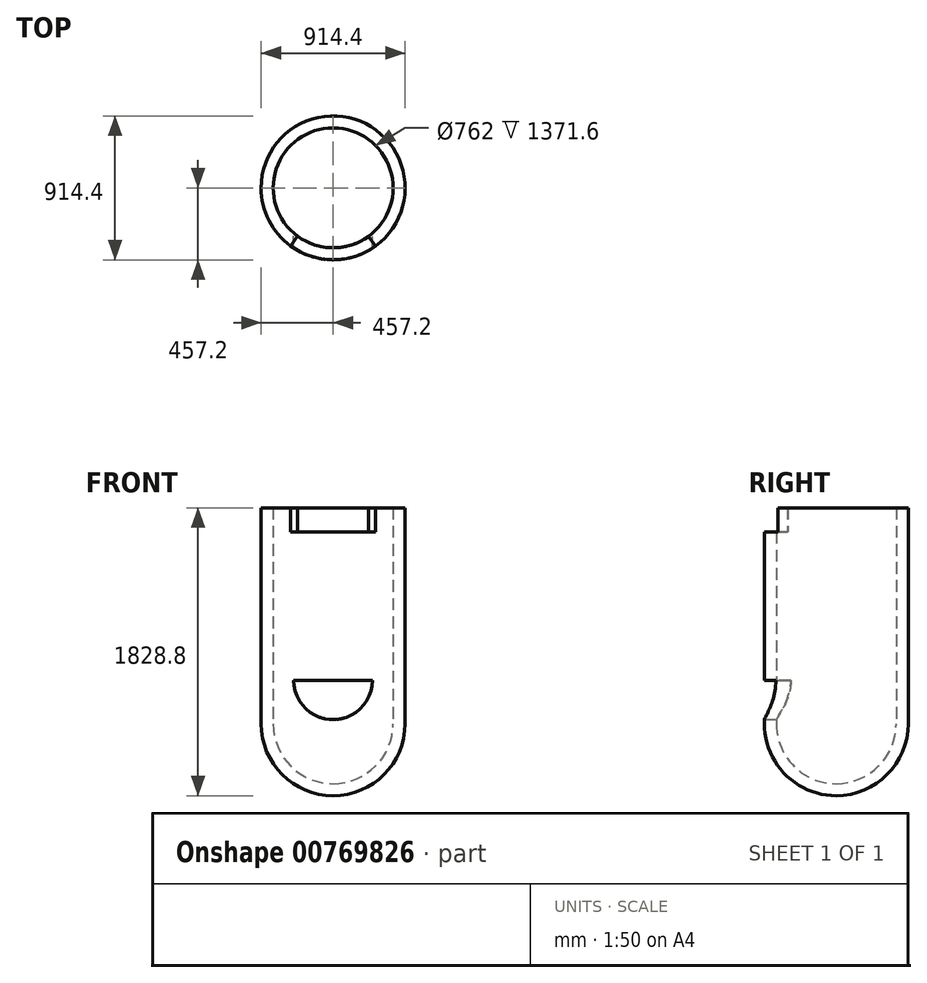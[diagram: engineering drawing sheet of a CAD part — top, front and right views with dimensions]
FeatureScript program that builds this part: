
annotation { "Feature Type Name" : "Feature", "Feature Type Description" : "" }
export const myFeature = defineFeature(function(context is Context, id is Id, definition is map)
    precondition{}
    {
        {
            var Q0;
            Q0=qCreatedBy(makeId("Top.planeOp"),FACE);
            var sketch = newSketch(context, id + "F0", { "sketchPlane" : qUnion([Q0])});
            skCircle(sketch, "E0", {"center": v(0, 0) * mm, "radius": 457.2 * mm});
            skCircle(sketch, "E1", {"center": v(0, 0) * mm, "radius": 381 * mm});
            skSolve(sketch);
        }
        {
            var Q0;
            Q0 = qSketchRegion(id + "F0", true);
            var Q1;
            Q1=makeQuery(id+"F0.imprint","IMPRINT",FACE,{"disambiguationData":[TD([[makeQuery(id+"F0.imprint","IMPRINT",EDGE,{"derivedFrom":sQuery(id+"F0.wireOp",EDGE,"E0")}),1.0]])]});
            extrude(context, id + "F1", {"entities" : qUnion([Q0, Q1]), "depth" : 1371.6 * mm, "offsetDistance" : 25.4 * mm});
        }
        {
            var Q0;
            Q0=qCreatedBy(makeId("Right.planeOp"),FACE);
            var sketch = newSketch(context, id + "F2", { "sketchPlane" : qUnion([Q0])});
            skArc(sketch, "E2", {"start": v(-381, 0) * mm, "mid": v(-269.4, -269.4) * mm, "end": v(0, -381) * mm});
            skArc(sketch, "E3", {"start": v(-457.2, 0) * mm, "mid": v(-323.29, -323.29) * mm, "end": v(0, -457.2) * mm});
            skLineSegment(sketch, "E4", {"start": v(0, -457.2) * mm, "end": v(0, -381) * mm});
            skLineSegment(sketch, "E5", {"start": v(0, -419.1) * mm, "end": v(0, -419.1) * mm});
            skLineSegment(sketch, "E6", {"start": v(-457.2, 0) * mm, "end": v(-381, 0) * mm});
            skSolve(sketch);
        }
        {
            var Q0;
            Q0 = qSketchRegion(id + "F2", true);
            var Q1;
            Q1=sQuery(id+"F2.wireOp",EDGE,"E4");
            revolve(context, id + "F3", {"operationType" : NewBodyOperationType.ADD, "surfaceOperationType" : NewSurfaceOperationType.NEW, "entities" : qUnion([Q0]), "axis" : qUnion([Q1]), "revolveType" : RevolveType.FULL});
        }
        {
            var Q0;
            Q0=qCreatedBy(makeId("Front.planeOp"),FACE);
            var sketch = newSketch(context, id + "F4", { "sketchPlane" : qUnion([Q0])});
            skLineSegment(sketch, "E7", {"start": v(249.4, 276.25) * mm, "end": v(-250.63, 276.25) * mm});
            skArc(sketch, "E8", {"start": v(249.4, 276.25) * mm, "mid": v(-0.62, 26.23) * mm, "end": v(-250.63, 276.25) * mm});
            skSolve(sketch);
        }
        {
            var Q0;
            Q0 = qSketchRegion(id + "F4", true);
            extrude(context, id + "F5", {"entities" : qUnion([Q0]), "operationType" : NewBodyOperationType.REMOVE, "depth" : 457.2 * mm, "offsetDistance" : 25.4 * mm});
        }
        {
            var Q0;
            Q0=qCreatedBy(makeId("Top.planeOp"),FACE);
            var sketch = newSketch(context, id + "F6", { "sketchPlane" : qUnion([Q0])});
            skLineSegment(sketch, "E9", {"start": v(0, 0) * mm, "end": v(-270.66, -368.48) * mm});
            skLineSegment(sketch, "E10", {"start": v(-270.66, -368.48) * mm, "end": v(-270.66, -368.48) * mm});
            skLineSegment(sketch, "E11", {"start": v(0, 0) * mm, "end": v(268.41, -370.12) * mm});
            skArc(sketch, "E12", {"start": v(268.41, -370.12) * mm, "mid": v(-1.54, -457.2) * mm, "end": v(-270.9, -368.3) * mm});
            skSolve(sketch);
        }
        {
            var Q0;
            Q0 = qSketchRegion(id + "F6", true);
            extrude(context, id + "F7", {"entities" : qUnion([Q0]), "operationType" : NewBodyOperationType.REMOVE, "depth" : 1371.6 * mm, "offsetDistance" : 25.4 * mm, "hasSecondDirection" : true, "secondDirectionOppositeDirection" : false, "secondDirectionDepth" : 1219.2 * mm});
        }
    });
